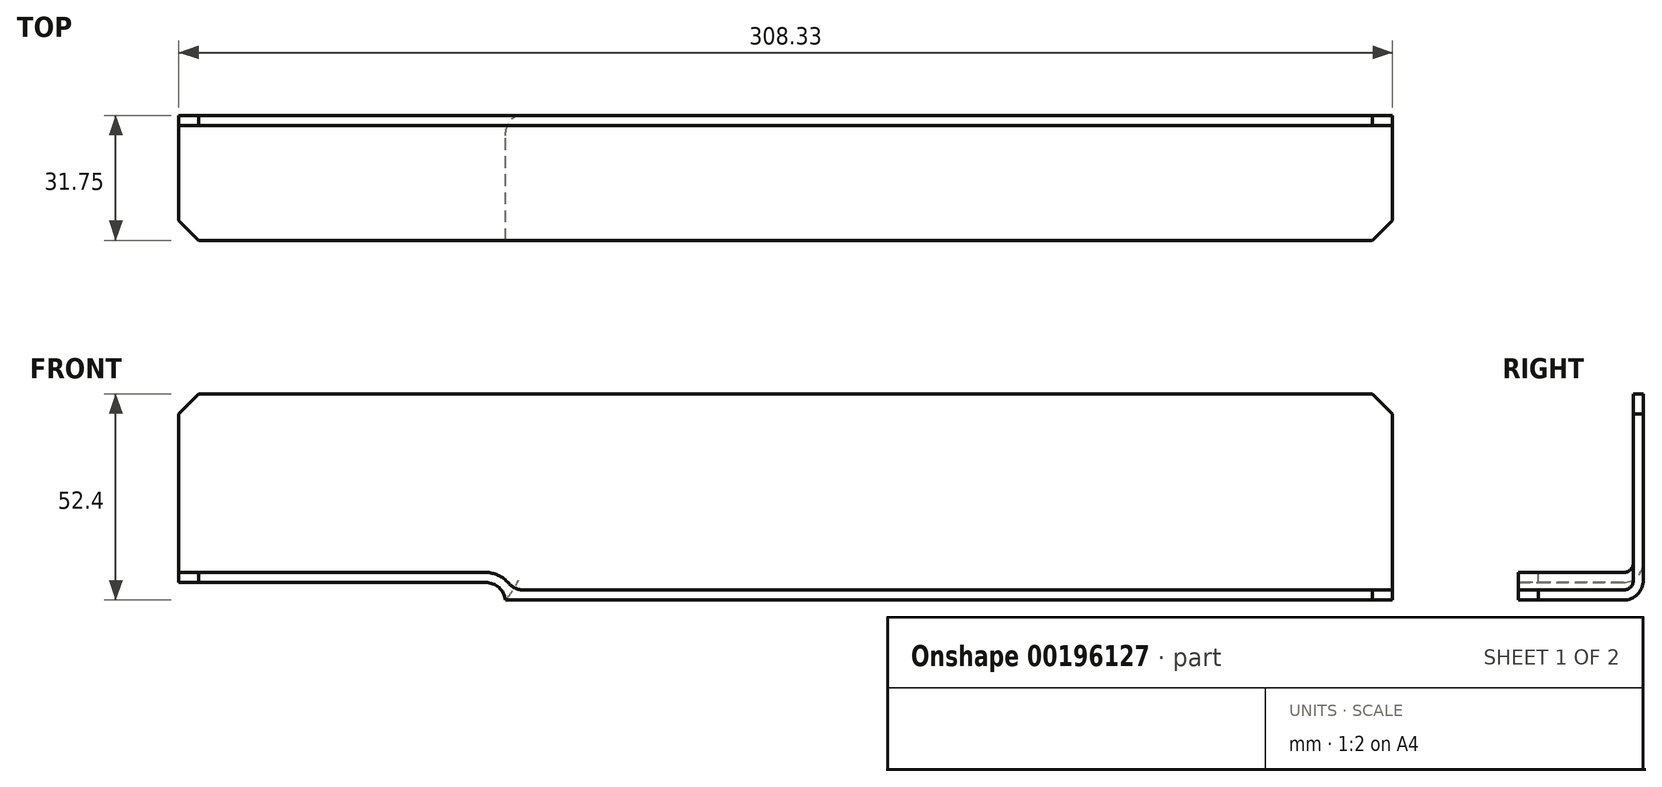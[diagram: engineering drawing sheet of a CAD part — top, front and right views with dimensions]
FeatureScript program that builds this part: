
annotation { "Feature Type Name" : "Feature", "Feature Type Description" : "" }
export const myFeature = defineFeature(function(context is Context, id is Id, definition is map)
    precondition{}
    {
        {
            var Q0;
            Q0=qCreatedBy(makeId("Front.planeOp"),FACE);
            var sketch = newSketch(context, id + "F0", { "sketchPlane" : qUnion([Q0])});
            skLineSegment(sketch, "E0.bottom", {"start": v(-176.7, 52.4) * mm, "end": v(131.63, 52.4) * mm});
            skLineSegment(sketch, "E0.top", {"start": v(-93.71, 0) * mm, "end": v(131.63, 0) * mm});
            skLineSegment(sketch, "E0.left", {"start": v(-176.7, 52.4) * mm, "end": v(-176.7, 4.47) * mm});
            skLineSegment(sketch, "E0.right", {"start": v(131.63, 52.4) * mm, "end": v(131.63, 0) * mm});
            skLineSegment(sketch, "E1", {"start": v(-176.7, 4.47) * mm, "end": v(-93.71, 4.47) * mm});
            skLineSegment(sketch, "E2", {"start": v(-93.71, 4.47) * mm, "end": v(-93.71, 0) * mm});
            skSolve(sketch);
        }
        {
            var Q0;
            Q0 = qSketchRegion(id + "F0", true);
            extrude(context, id + "F1", {"entities" : qUnion([Q0]), "depth" : 31.75 * mm});
        }
        {
            var Q0;
            Q0=makeQuery(id+"F1.opExtrude","SWEPT_EDGE",EDGE,{"disambiguationData":[OSD([sQuery(id+"F0.wireOp",EDGE,"E1"),sQuery(id+"F0.wireOp",EDGE,"E2")])]});
            fillet(context, id + "F2", {"entities" : qUnion([Q0]), "radius" : 5.08 * mm, "tangentPropagation" : true, "allowEdgeOverflow" : false});
        }
        {
            var Q0;
            Q0=makeQuery(id+"F1.opExtrude","CAP_EDGE",EDGE,{"disambiguationData":[OSD([sQuery(id+"F0.wireOp",EDGE,"E1")])],"isStart":true});
            var Q1;
            Q1=makeQuery(id+"F1.opExtrude","CAP_EDGE",EDGE,{"disambiguationData":[OSD([sQuery(id+"F0.wireOp",EDGE,"E0.top")])],"isStart":true});
            fillet(context, id + "F3", {"entities" : qUnion([Q0, Q1]), "radius" : 5.08 * mm, "tangentPropagation" : true, "allowEdgeOverflow" : false});
        }
        {
            var Q0;
            Q0=makeQuery(id+"F1.opExtrude","SWEPT_FACE",FACE,{"disambiguationData":[OSD([sQuery(id+"F0.wireOp",EDGE,"E0.bottom")])]});
            var Q1;
            Q1=makeQuery(id+"F1.opExtrude","CAP_FACE",FACE,{"disambiguationData":[OSD([sQuery(id+"F0.wireOp",EDGE,"E0.bottom"),sQuery(id+"F0.wireOp",EDGE,"E0.top"),sQuery(id+"F0.wireOp",EDGE,"E0.left"),sQuery(id+"F0.wireOp",EDGE,"E0.right"),sQuery(id+"F0.wireOp",EDGE,"E1"),sQuery(id+"F0.wireOp",EDGE,"E2")])],"isStart":false});
            var Q2;
            Q2=makeQuery(id+"F1.opExtrude","SWEPT_FACE",FACE,{"disambiguationData":[OSD([sQuery(id+"F0.wireOp",EDGE,"E0.left")])]});
            var Q3;
            Q3=makeQuery(id+"F1.opExtrude","SWEPT_FACE",FACE,{"disambiguationData":[OSD([sQuery(id+"F0.wireOp",EDGE,"E0.right")])]});
            shell(context, id + "F4", {"entities" : qUnion([Q0, Q1, Q2, Q3]), "thickness" : 2.54 * mm});
        }
        {
            var Q0;
            Q0=makeQuery(id+"F4.opShell","OFFSET_EDGE",EDGE,{"disambiguationData":[OSD([sQuery(id+"F0.wireOp",EDGE,"E0.top"),sQuery(id+"F0.wireOp",EDGE,"E1"),sQuery(id+"F0.wireOp",EDGE,"E2")])]});
            fillet(context, id + "F5", {"entities" : qUnion([Q0]), "radius" : 5.08 * mm, "tangentPropagation" : true, "allowEdgeOverflow" : false});
        }
        {
            var Q0;
            Q0=makeQuery(id+"F1.opExtrude","SWEPT_EDGE",EDGE,{"disambiguationData":[OSD([sQuery(id+"F0.wireOp",EDGE,"E0.bottom"),sQuery(id+"F0.wireOp",EDGE,"E0.left")])]});
            var Q1;
            Q1=makeQuery(id+"F1.opExtrude","CAP_EDGE",EDGE,{"disambiguationData":[OSD([sQuery(id+"F0.wireOp",EDGE,"E0.left")])],"isStart":false});
            var Q2;
            Q2=makeQuery(id+"F1.opExtrude","SWEPT_EDGE",EDGE,{"disambiguationData":[OSD([sQuery(id+"F0.wireOp",EDGE,"E0.bottom"),sQuery(id+"F0.wireOp",EDGE,"E0.right")])]});
            var Q3;
            Q3=makeQuery(id+"F1.opExtrude","CAP_EDGE",EDGE,{"disambiguationData":[OSD([sQuery(id+"F0.wireOp",EDGE,"E0.right")])],"isStart":false});
            chamfer(context, id + "F6", {"entities" : qUnion([Q0, Q1, Q2, Q3]), "width" : 5.08 * mm, "tangentPropagation" : true});
        }
    });
